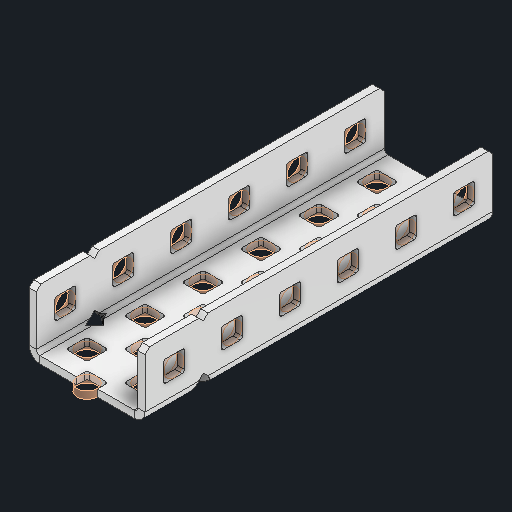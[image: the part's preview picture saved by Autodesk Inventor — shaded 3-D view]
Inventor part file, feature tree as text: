
AUTODESK INVENTOR PART (.ipt)
format: ipt  version: 2025 (Build 290162000, 162)  size: 676,352 bytes
history: native  units: in
note: dims shown in document units (in); Inventor stores cm internally (conversion verified against a paired STEP export)
features: other x66, sketch x5, sheet_metal_op x1
ambient origin geometry x8: Origin, YZ Plane, XZ Plane, XY Plane, X Axis, Y Axis, Z Axis, Center Point
bodies: Solid1 (feature_tree)
feature tree (72):
  other  "Alu C 1x2x1x6.ipt"
  other  "Solid1::Alu C 1x2x1x6.ipt"
  other  "TaggingFeature1"
  sketch  "Sketch1"  dims[d0=0.3937in]
  sketch  "Sketch2"  dims[d1=0.0625in]
  sketch  "Sketch3"
  other  "Flange Pattern Sketch"
  sketch  "Sketch9"
  sheet_metal_op  "Body Pattern Sketch"
  other  "Arc Length"
  sketch  "Sketch14"
  other  "Flange Pattern Plane"
  other  "Srf1"
  other  "Srf2"
  other  "Srf3"
  other  "Srf4"
  other  "Srf5"
  other  "Srf6"
  other  "Srf7"
  other  "Srf8"
  other  "Srf9"
  other  "Srf10"
  other  "Srf11"
  other  "Srf12"
  other  "Srf13"
  other  "Srf14"
  other  "Srf15"
  other  "Srf16"
  other  "Srf17"
  other  "Srf18"
  other  "Srf19"
  other  "Srf20"
  other  "Srf21"
  other  "Srf22"
  other  "Srf23"
  other  "Srf24"
  other  "Srf25"
  other  "Srf26"
  other  "Srf27"
  other  "Srf28"
  other  "Srf29"
  other  "Srf30"
  other  "Srf1::Derived"
  other  "Srf2::Derived"
  other  "Srf823::Derived"
  other  "Srf824::Derived"
  other  "Srf825::Derived"
  other  "Srf826::Derived"
  other  "Srf827::Derived"
  other  "Srf828::Derived"
  other  "Srf829::Derived"
  other  "Srf922::Derived"
  other  "Srf923::Derived"
  other  "Srf924::Derived"
  other  "Srf91::Derived"
  other  "Srf92::Derived"
  other  "Srf856::Derived"
  other  "Srf857::Derived"
  other  "Srf858::Derived"
  other  "Srf859::Derived"
  other  "Srf860::Derived"
  other  "Srf861::Derived"
  other  "Srf862::Derived"
  other  "Srf959::Derived"
  other  "Srf960::Derived"
  other  "Srf961::Derived"
  other  "Srf786::Derived"
  other  "Srf889::Derived"
  other  "Srf890::Derived"
  other  "Srf891::Derived"
  other  "Srf892::Derived"
  other  "Srf893::Derived"
